# Revit family: EDLR-E2-150-xxxx-8xx-WS
name_source: partatom
category: Oprawy oświetleniowe
revit_build: Autodesk Revit 2017 (Build: 20190507_1515(x64)
units: mm (PartAtom-declared; Revit-internal decimal feet)

## family parameters
Numer OmniClass = 23.80.70.11
Obiekt nadrzędny = Powierzchnia
Punkt obliczania pomieszczeń = Nie
Tnij formami wycięć po wczytaniu = Tak
Typ części = Normalny
Tytuł OmniClass = Luminaries for Internal Lighting
Współdzielony = Nie
Wymiar okrągłego złącza = Użyj średnicy
Źródło światła = Tak

## types (8) — shared parameters
Emituj kształt widoczny w renderingu = Nie
Emituj ze średnicy okręgu = 130 mm  [stored 0.426509 ft]
Filtr koloru = 16777215
Kod zespołu = D5020200
Lampa = LED
Odchylenie kierunku = 90.00°
Producent = RIDI Leuchten GmbH
URL = www.ridi.de
Zmiana temperatury barwowej przyciemniania lampy = <Brak>
brand = RIDI
conformity mark = CE
electrical safety class = 1
height = 60 mm  [stored 0.19685 ft]
ingress protection (IP) code = IP20
length = 150 mm
nominal frequency = 50-60Hz
nominal voltage = 230
voltage type (AC, DC, UC) = AC
width = 150 mm
zero-valued in all types: Domyślna rzędna

## per-type parameters (varying)
| type | Model | Obciążenie pozorne | Plik sieci fotometrycznej | rated input power | weight |
| EDLR-E2 150/1100-830 WS | 0326633 | 9 VA | EDLR-E2 150_1100-840 WS.IES | 9 | 0.37kg |
| EDLR-E2 150/1100-830 WS-DALI | 0336633 | 9 VA | EDLR-E2 150_1100-840 WS.IES | 9 | 0.483kg |
| EDLR-E2 150/1100-840 WS | 0326632 | 9 VA | EDLR-E2 150_1100-840 WS.IES | 9 | 0.37kg |
| EDLR-E2 150/1100-840 WS-DALI | 0336632 | 9 VA | EDLR-E2 150_1100-840 WS.IES | 9 | 0.483kg |
| EDLR-E2 150/2000-830 WS | 0326635 | 16 VA | EDLR-E2 150_2000-840 WS.IES | 16 | 0.37kg |
| EDLR-E2 150/2000-830 WS-DALI | 0336635 | 16 VA | EDLR-E2 150_2000-840 WS.IES | 16 | 0.483kg |
| EDLR-E2 150/2000-840 WS | 0326634 | 16 VA | EDLR-E2 150_2000-840 WS.IES | 16 | 0.37kg |
| EDLR-E2 150/2000-840 WS-DALI | 0336634 | 16 VA | EDLR-E2 150_2000-840 WS.IES | 16 | 0.483kg |

note: column(s) folded — value = type name in every type: product name

note: [stored X ft] marks values corroborated as IEEE doubles in the binary element streams (Revit-internal decimal feet)
